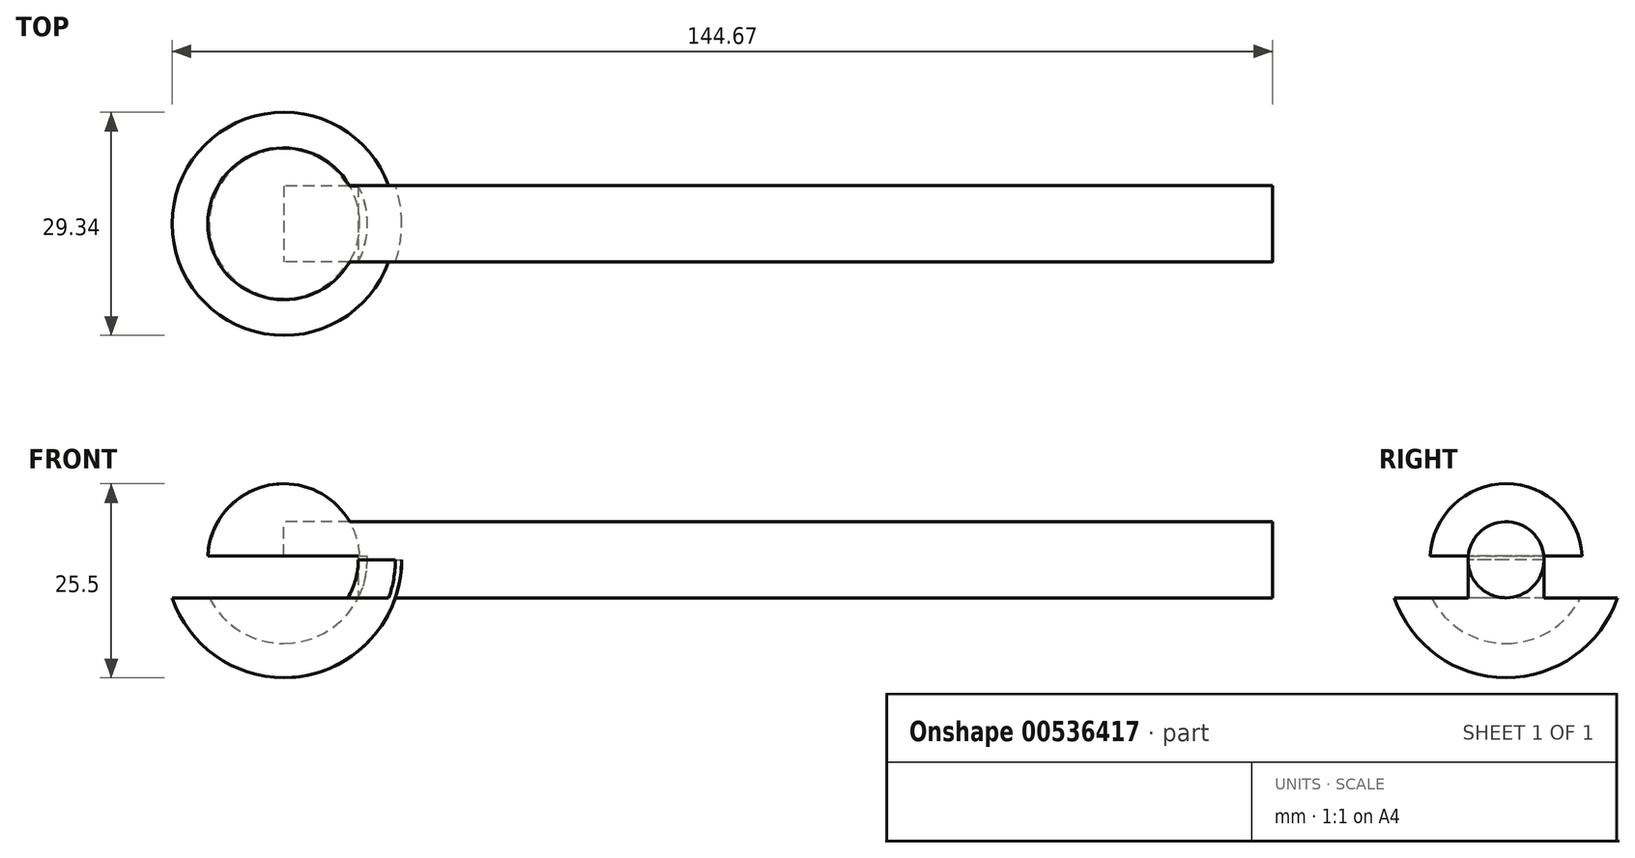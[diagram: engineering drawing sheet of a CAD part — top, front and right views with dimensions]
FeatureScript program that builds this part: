
annotation { "Feature Type Name" : "Feature", "Feature Type Description" : "" }
export const myFeature = defineFeature(function(context is Context, id is Id, definition is map)
    precondition{}
    {
        {
            var Q0;
            Q0=qCreatedBy(makeId("Front.planeOp"),FACE);
            var sketch = newSketch(context, id + "F0", { "sketchPlane" : qUnion([Q0])});
            skArc(sketch, "E0", {"start": v(0, -10) * mm, "mid": v(10, 0) * mm, "end": v(0, 10) * mm});
            skLineSegment(sketch, "E1", {"start": v(0, 10) * mm, "end": v(0, -10) * mm});
            skSolve(sketch);
        }
        {
            var Q0;
            Q0 = qSketchRegion(id + "F0", true);
            var Q1;
            Q1=sQuery(id+"F0.wireOp",EDGE,"E1");
            revolve(context, id + "F1", {"entities" : qUnion([Q0]), "axis" : qUnion([Q1]), "revolveType" : RevolveType.FULL});
        }
        {
            var Q0;
            Q0=qCreatedBy(makeId("Top.planeOp"),FACE);
            var sketch = newSketch(context, id + "F2", { "sketchPlane" : qUnion([Q0])});
            skCircle(sketch, "E2", {"center": v(0, 0) * mm, "radius": 10 * mm});
            skSolve(sketch);
        }
        {
            var Q0;
            Q0 = qSketchRegion(id + "F2", true);
            extrude(context, id + "F3", {"entities" : qUnion([Q0]), "operationType" : NewBodyOperationType.REMOVE, "depth" : 0.5 * mm, "offsetDistance" : 25 * mm, "hasSecondDirection" : true, "secondDirectionBound" : SecondDirectionBoundingType.THROUGH_ALL, "secondDirectionOppositeDirection" : true, "secondDirectionDepth" : 25 * mm});
        }
        {
            var Q0;
            Q0=qCreatedBy(makeId("Front.planeOp"),FACE);
            var sketch = newSketch(context, id + "F4", { "sketchPlane" : qUnion([Q0])});
            skArc(sketch, "E3", {"start": v(0, -11) * mm, "mid": v(7.78, -7.78) * mm, "end": v(11, 0) * mm});
            skArc(sketch, "E4", {"start": v(0, -15.5) * mm, "mid": v(10.96, -10.96) * mm, "end": v(15.5, 0) * mm});
            skLineSegment(sketch, "E5.trimOffspring", {"start": v(11, 0) * mm, "end": v(15.5, 0) * mm});
            skLineSegment(sketch, "E6", {"start": v(0, -15.5) * mm, "end": v(0, -11) * mm});
            skSolve(sketch);
        }
        {
            var Q0;
            Q0 = qSketchRegion(id + "F4", true);
            var Q1;
            Q1=sQuery(id+"F4.wireOp",EDGE,"E6");
            revolve(context, id + "F5", {"entities" : qUnion([Q0]), "axis" : qUnion([Q1]), "revolveType" : RevolveType.FULL});
        }
        {
            var Q0;
            Q0=qCreatedBy(makeId("Right.planeOp"),FACE);
            var sketch = newSketch(context, id + "F6", { "sketchPlane" : qUnion([Q0])});
            skCircle(sketch, "E7", {"center": v(0, 0) * mm, "radius": 5 * mm});
            skSolve(sketch);
        }
        {
            var Q0;
            Q0 = qSketchRegion(id + "F6", true);
            extrude(context, id + "F7", {"entities" : qUnion([Q0]), "depth" : 130 * mm, "offsetDistance" : 25 * mm});
        }
        {
            var Q0;
            Q0=qCreatedBy(makeId("Front.planeOp"),FACE);
            var sketch = newSketch(context, id + "F8", { "sketchPlane" : qUnion([Q0])});
            skArc(sketch, "E8", {"start": v(0, -11) * mm, "mid": v(7.95, -7.6) * mm, "end": v(10.99, 0.5) * mm});
            skLineSegment(sketch, "E9", {"start": v(0, -11) * mm, "end": v(0, 0.5) * mm});
            skLineSegment(sketch, "E10", {"start": v(0, 0.5) * mm, "end": v(10.99, 0.5) * mm});
            skSolve(sketch);
        }
        {
            var Q0;
            Q0 = qSketchRegion(id + "F8", true);
            var Q1;
            Q1=sQuery(id+"F8.wireOp",EDGE,"E9");
            revolve(context, id + "F9", {"operationType" : NewBodyOperationType.REMOVE, "entities" : qUnion([Q0]), "axis" : qUnion([Q1]), "revolveType" : RevolveType.FULL, "oppositeDirection" : true});
        }
        {
            var Q0;
            Q0=qCreatedBy(makeId("Top.planeOp"),FACE);
            var sketch = newSketch(context, id + "F10", { "sketchPlane" : qUnion([Q0])});
            skArc(sketch, "E11", {"start": v(14.67, 5) * mm, "mid": v(-15.5, 0) * mm, "end": v(14.67, -5) * mm});
            skLineSegment(sketch, "E12", {"start": v(14.67, 5) * mm, "end": v(0, 5) * mm});
            skLineSegment(sketch, "E13", {"start": v(0, 5) * mm, "end": v(0, -5) * mm});
            skLineSegment(sketch, "E14", {"start": v(0, -5) * mm, "end": v(14.67, -5) * mm});
            skSolve(sketch);
        }
        {
            var Q0;
            Q0 = qSketchRegion(id + "F10", true);
            extrude(context, id + "F11", {"entities" : qUnion([Q0]), "operationType" : NewBodyOperationType.REMOVE, "oppositeDirection" : true, "depth" : 5 * mm, "offsetDistance" : 25 * mm});
        }
    });
